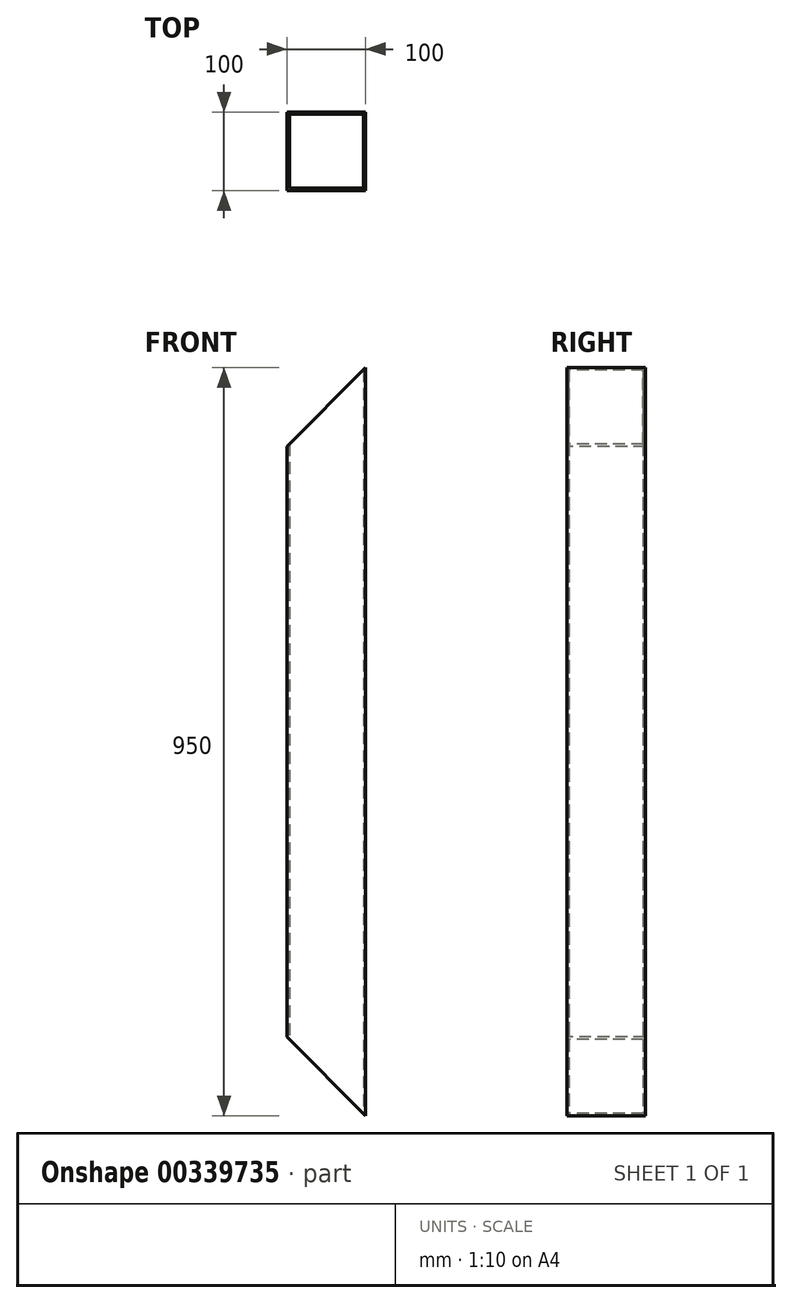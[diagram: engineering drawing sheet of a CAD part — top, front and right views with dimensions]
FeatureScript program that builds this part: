
annotation { "Feature Type Name" : "Feature", "Feature Type Description" : "" }
export const myFeature = defineFeature(function(context is Context, id is Id, definition is map)
    precondition{}
    {
        {
            var Q0;
            Q0=qCreatedBy(makeId("Top.planeOp"),FACE);
            var sketch = newSketch(context, id + "F0", { "sketchPlane" : qUnion([Q0])});
            skLineSegment(sketch, "E0.bottom", {"start": v(-46.4, 36.2) * mm, "end": v(53.6, 36.2) * mm});
            skLineSegment(sketch, "E0.top", {"start": v(-46.4, -63.8) * mm, "end": v(53.6, -63.8) * mm});
            skLineSegment(sketch, "E0.left", {"start": v(-46.4, 36.2) * mm, "end": v(-46.4, -63.8) * mm});
            skLineSegment(sketch, "E0.right", {"start": v(53.6, 36.2) * mm, "end": v(53.6, -63.8) * mm});
            skLineSegment(sketch, "E1.bottom", {"start": v(-43.4, 33.2) * mm, "end": v(50.6, 33.2) * mm});
            skLineSegment(sketch, "E1.top", {"start": v(-43.4, -60.8) * mm, "end": v(50.6, -60.8) * mm});
            skLineSegment(sketch, "E1.left", {"start": v(-43.4, 33.2) * mm, "end": v(-43.4, -60.8) * mm});
            skLineSegment(sketch, "E1.right", {"start": v(50.6, 33.2) * mm, "end": v(50.6, -60.8) * mm});
            skSolve(sketch);
        }
        {
            var Q0;
            Q0 = qSketchRegion(id + "F0", true);
            extrude(context, id + "F1", {"entities" : qUnion([Q0]), "depth" : 950 * mm});
        }
        {
            var Q0;
            Q0=makeQuery(id+"F1.opExtrude","SWEPT_FACE",FACE,{"disambiguationData":[OSD([sQuery(id+"F0.wireOp",EDGE,"E0.top")])]});
            var sketch = newSketch(context, id + "F2", { "sketchPlane" : qUnion([Q0])});
            skLineSegment(sketch, "E2", {"start": v(53.6, 950) * mm, "end": v(-148.2, 748.2) * mm});
            skSolve(sketch);
        }
        {
            var Q0;
            {var subQ1=sQuery(id+"F0.wireOp",EDGE,"E0.top");var subQ2=makeQuery(id+"F1.opExtrude","CAP_EDGE",EDGE,{"disambiguationData":[OSD([subQ1])],"isStart":false});Q0=makeQuery(id+"F2.imprint","IMPRINT",FACE,{"disambiguationData":[TD([[makeQuery(id+"F2.imprint","IMPRINT",EDGE,{"derivedFrom":subQ2}),-1.0]])]});}
            extrude(context, id + "F3", {"entities" : qUnion([Q0]), "operationType" : NewBodyOperationType.REMOVE, "oppositeDirection" : true, "depth" : 100 * mm});
        }
        {
            var Q0;
            Q0=makeQuery(id+"F1.opExtrude","SWEPT_FACE",FACE,{"disambiguationData":[OSD([sQuery(id+"F0.wireOp",EDGE,"E0.top")])]});
            var sketch = newSketch(context, id + "F4", { "sketchPlane" : qUnion([Q0])});
            skLineSegment(sketch, "E3", {"start": v(53.6, 0) * mm, "end": v(-266.05, 319.65) * mm});
            skSolve(sketch);
        }
        {
            var Q0;
            Q0 = qSketchRegion(id + "F4", true);
            var Q1;
            {var subQ1=sQuery(id+"F0.wireOp",EDGE,"E0.top");var subQ2=makeQuery(id+"F1.opExtrude","CAP_EDGE",EDGE,{"disambiguationData":[OSD([subQ1])],"isStart":true});Q1=makeQuery(id+"F4.imprint","IMPRINT",FACE,{"disambiguationData":[TD([[makeQuery(id+"F4.imprint","IMPRINT",EDGE,{"derivedFrom":subQ2}),1.0]])]});}
            extrude(context, id + "F5", {"entities" : qUnion([Q0, Q1]), "operationType" : NewBodyOperationType.REMOVE, "oppositeDirection" : true, "depth" : 100 * mm});
        }
    });
